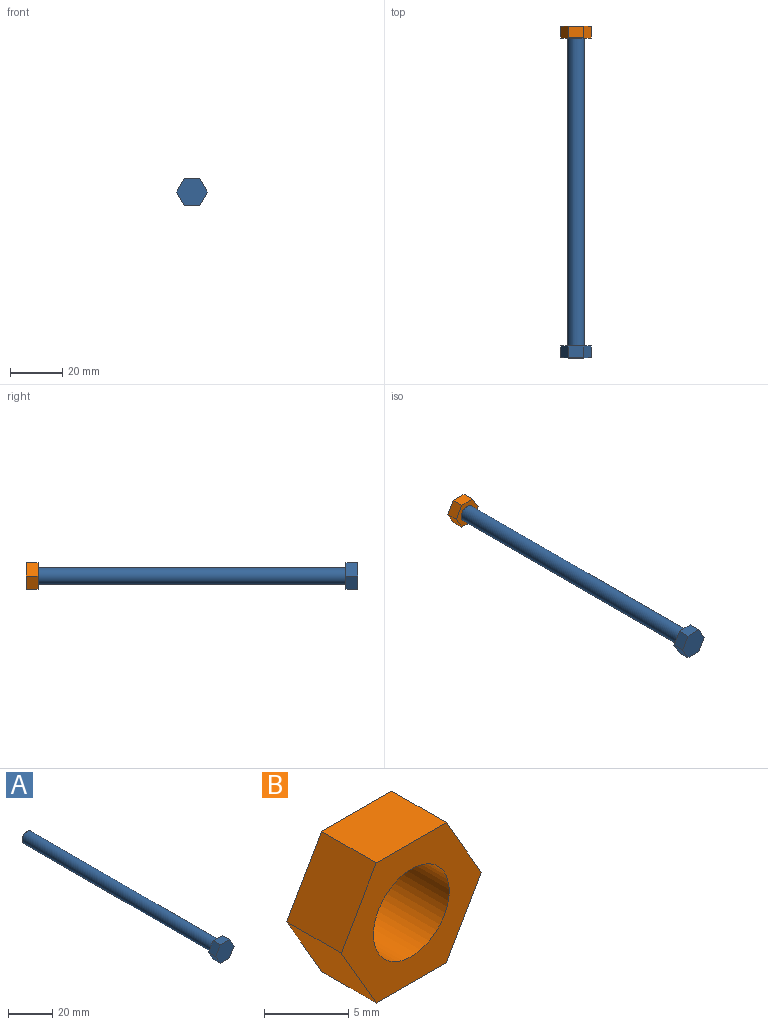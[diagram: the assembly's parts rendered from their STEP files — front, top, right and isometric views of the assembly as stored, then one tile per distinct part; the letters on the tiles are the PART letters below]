
ASSEMBLY  parts=2 mates=1
PART A: 10 faces, bbox 11.7x126.5x10.2 mm
  f0: cylinder r=3.17mm len=121.92mm, axis (0,1,0), area 2432.2mm2, adj f1,f9
  f1: plane 6.35x6.35mm, normal (0,1,0), area 31.7mm2, adj f0
  f2: plane 5.08x4.57mm, normal (0.87,0,0.5), area 26.8mm2, adj f3,f7,f8,f9
  f3: plane 5.87x4.57mm, normal (0,0,1), area 26.8mm2, adj f2,f4,f8,f9
  f4: plane 5.08x4.57mm, normal (-0.87,0,0.5), area 26.8mm2, adj f3,f5,f8,f9
  f5: plane 5.08x4.57mm, normal (-0.87,0,-0.5), area 26.8mm2, adj f4,f6,f8,f9
  f6: plane 5.87x4.57mm, normal (0,0,-1), area 26.8mm2, adj f5,f7,f8,f9
  f7: plane 5.08x4.57mm, normal (0.87,0,-0.5), area 26.8mm2, adj f2,f6,f8,f9
  f8: plane 11.73x10.16mm, normal (0,-1,0), area 89.4mm2, adj f2,f3,f4,f5,f6,f7
  f9: plane 11.73x10.16mm, normal (0,1,0), area 57.7mm2, adj f0,f2,f3,f4,f5,f6,f7
PART B: 9 faces, bbox 11.7x4.6x10.2 mm
  f0: plane 5.08x4.57mm, normal (0.87,0,0.5), area 26.8mm2, adj f1,f5,f6,f7
  f1: plane 5.87x4.57mm, normal (0,0,1), area 26.8mm2, adj f0,f2,f6,f7
  f2: plane 5.08x4.57mm, normal (-0.87,0,0.5), area 26.8mm2, adj f1,f3,f6,f7
  f3: plane 5.08x4.57mm, normal (-0.87,0,-0.5), area 26.8mm2, adj f2,f4,f6,f7
  f4: plane 5.87x4.57mm, normal (0,0,-1), area 26.8mm2, adj f3,f5,f6,f7
  f5: plane 5.08x4.57mm, normal (0.87,0,-0.5), area 26.8mm2, adj f0,f4,f6,f7
  f6: plane 11.73x10.16mm, normal (0,-1,0), area 57.7mm2, adj f0,f1,f2,f3,f4,f5,f8
  f7: plane 11.73x10.16mm, normal (0,1,0), area 57.7mm2, adj f0,f1,f2,f3,f4,f5,f8
  f8: cylinder r=3.17mm len=6.35mm, axis (0,1,0), area 91.2mm2, adj f6,f7
PLACE A t=(0,-67.06,0)mm
PLACE B t=(0,-6.1,0)mm
MATE fastened A.f0 <-> B.f8  axis (0,1,0) through (0,-6.1,0)mm
